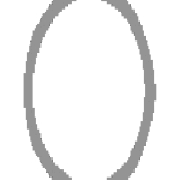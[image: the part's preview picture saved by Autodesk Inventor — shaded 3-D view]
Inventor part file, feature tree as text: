
AUTODESK INVENTOR PART (.ipt)
format: ipt  version: 2021 (Build 250183000, 183)  size: 110,080 bytes
history: native  units: in
note: dims shown in document units (in); Inventor stores cm internally (conversion verified against a paired STEP export)
features: other x4, sketch x3, plane x1
ambient origin geometry x8: Origin, YZ Plane, XZ Plane, XY Plane, X Axis, Y Axis, Z Axis, Center Point
bodies: Solid1 (feature_tree), Body (feature_tree)
feature tree (8):
  other  "Driven Length"
  other  "Frame Generator"
  other  "Start Plane"
  other  "End Plane"
  sketch  "Sketch"  dims[d2=16.0in d4=-0.0in d5=16.0in d6=0.12in d7=0.0in d8=90.0deg d9=16.0in]
  sketch  "Sketch2"  dims[d0=1.0in]
  plane  "Work Plane3"
  sketch  "Sketch3"  dims[d1=0.065in]
